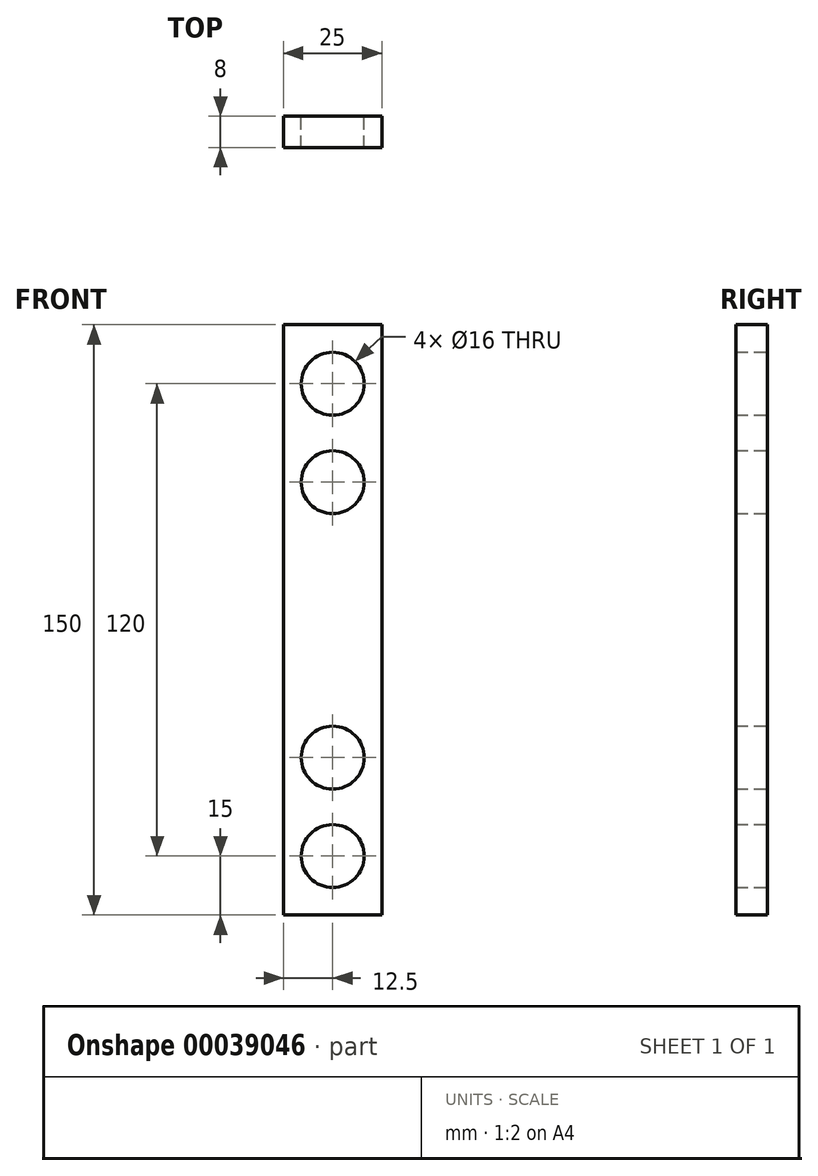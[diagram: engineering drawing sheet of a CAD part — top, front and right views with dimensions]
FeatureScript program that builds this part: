
annotation { "Feature Type Name" : "Feature", "Feature Type Description" : "" }
export const myFeature = defineFeature(function(context is Context, id is Id, definition is map)
    precondition{}
    {
        {
            var Q0;
            Q0=qCreatedBy(makeId("Front.planeOp"),FACE);
            var sketch = newSketch(context, id + "F0", { "sketchPlane" : qUnion([Q0])});
            skLineSegment(sketch, "E0.0", {"start": v(-12.5, 75) * mm, "end": v(-12.5, -75) * mm});
            skLineSegment(sketch, "E1.0", {"start": v(12.5, 75) * mm, "end": v(12.5, -75) * mm});
            skLineSegment(sketch, "E2.0", {"start": v(12.5, -75) * mm, "end": v(-12.5, -75) * mm});
            skLineSegment(sketch, "E3.0", {"start": v(-12.5, 75) * mm, "end": v(12.5, 75) * mm});
            skCircle(sketch, "E4.0", {"center": v(0, 60) * mm, "radius": 8 * mm});
            skLineSegment(sketch, "E5.0.0", {"start": v(-12.5, -75) * mm, "end": v(12.5, -75) * mm});
            skLineSegment(sketch, "E5.0.1", {"start": v(12.5, -75) * mm, "end": v(12.5, 75) * mm});
            skLineSegment(sketch, "E5.0.2", {"start": v(12.5, 75) * mm, "end": v(-12.5, 75) * mm});
            skCircle(sketch, "E6.0", {"center": v(0, -35) * mm, "radius": 8 * mm});
            skCircle(sketch, "E7.0", {"center": v(0, -60) * mm, "radius": 8 * mm});
            skCircle(sketch, "E8.0", {"center": v(0, 35) * mm, "radius": 8 * mm});
            skSolve(sketch);
        }
        {
            var Q0;
            Q0 = qSketchRegion(id + "F0", true);
            extrude(context, id + "F1", {"entities" : qUnion([Q0]), "depth" : 8 * mm});
        }
    });
